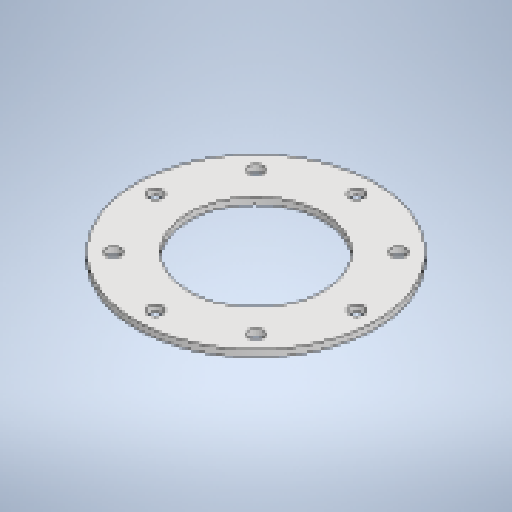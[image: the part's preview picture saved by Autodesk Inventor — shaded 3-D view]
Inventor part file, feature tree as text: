
AUTODESK INVENTOR PART (.ipt)
format: ipt  version: 2025.1 (Build 291241020, 241B)  size: 207,360 bytes
history: native  units: mm
features: other x3, sketch x2, sheet_metal_op x1, pattern_circular x1
ambient origin geometry x8: Origin, YZ Plane, XZ Plane, XY Plane, X Axis, Y Axis, Z Axis, Center Point
bodies: Body1 (feature_tree)
feature tree (7):
  sheet_metal_op  "Face2"
  pattern_circular  "Circular Pattern1"  [2 undecoded]
  sketch  "Sketch2"  dims[d14=8.0mm]
  other  "Plate2"
  sketch  "Sketch3"  dims[d15=17.0mm d17=8.0mm d18=0.0mm d19=80.0mm d20=360.0deg d25=161.0mm d27=285.0mm d28=240.0mm]
  other  "Cut1"
  other  "Definition1"
note: 2 required parameter values undecoded (feature->parameter linkage not recoverable at this tier; creation-order binding heuristic only, values carry confidence <= 0.55)
